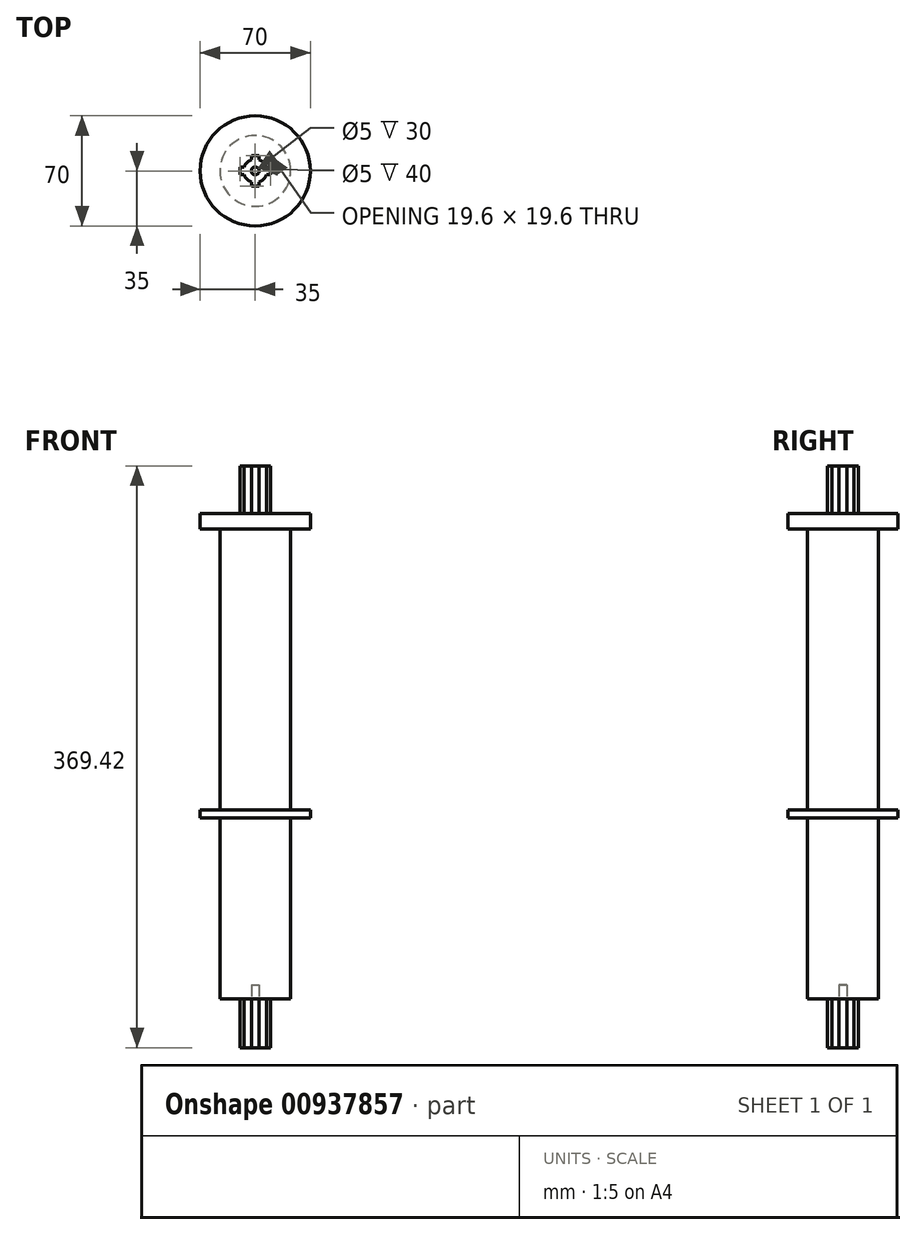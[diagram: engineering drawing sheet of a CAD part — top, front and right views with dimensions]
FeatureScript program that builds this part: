
annotation { "Feature Type Name" : "Feature", "Feature Type Description" : "" }
export const myFeature = defineFeature(function(context is Context, id is Id, definition is map)
    precondition{}
    {
        {
            var Q0;
            Q0=qCreatedBy(makeId("Top.planeOp"),FACE);
            var sketch = newSketch(context, id + "F0", { "sketchPlane" : qUnion([Q0])});
            skCircle(sketch, "E0", {"center": v(0, 0) * mm, "radius": 22.5 * mm});
            skSolve(sketch);
        }
        {
            var Q0;
            Q0=makeQuery(id+"F0.imprint","IMPRINT",FACE,{"disambiguationData":[TD([[makeQuery(id+"F0.imprint","IMPRINT",EDGE,{"derivedFrom":sQuery(id+"F0.wireOp",EDGE,"E0")}),1.0]])]});
            extrude(context, id + "F1", {"entities" : qUnion([Q0]), "depth" : 308.42 * mm, "offsetDistance" : 25 * mm});
        }
        {
            var Q0;
            Q0=makeQuery(id+"F1.opExtrude","CAP_FACE",FACE,{"disambiguationData":[OSD([sQuery(id+"F0.wireOp",EDGE,"E0")])],"isStart":false});
            var sketch = newSketch(context, id + "F2", { "sketchPlane" : qUnion([Q0])});
            skCircle(sketch, "E1", {"center": v(0, 0) * mm, "radius": 7.5 * mm});
            skLineSegment(sketch, "E2", {"start": v(0, 9.8) * mm, "end": v(-2.5, 9.8) * mm});
            skLineSegment(sketch, "E3", {"start": v(0, 9.8) * mm, "end": v(2.5, 9.8) * mm});
            skLineSegment(sketch, "E4", {"start": v(2.5, 9.8) * mm, "end": v(2.5, 7.07) * mm});
            skLineSegment(sketch, "E5", {"start": v(-2.5, 9.8) * mm, "end": v(-2.5, 7.07) * mm});
            skLineSegment(sketch, "E6.1.0", {"start": v(-9.8, 0) * mm, "end": v(-9.8, 2.5) * mm});
            skLineSegment(sketch, "E6.1.1", {"start": v(-9.8, 2.5) * mm, "end": v(-7.07, 2.5) * mm});
            skLineSegment(sketch, "E6.1.2", {"start": v(-9.8, 0) * mm, "end": v(-9.8, -2.5) * mm});
            skLineSegment(sketch, "E6.1.3", {"start": v(-9.8, -2.5) * mm, "end": v(-7.07, -2.5) * mm});
            skLineSegment(sketch, "E6.2.0", {"start": v(0, -9.8) * mm, "end": v(-2.5, -9.8) * mm});
            skLineSegment(sketch, "E6.2.1", {"start": v(-2.5, -9.8) * mm, "end": v(-2.5, -7.07) * mm});
            skLineSegment(sketch, "E6.2.2", {"start": v(0, -9.8) * mm, "end": v(2.5, -9.8) * mm});
            skLineSegment(sketch, "E6.2.3", {"start": v(2.5, -9.8) * mm, "end": v(2.5, -7.07) * mm});
            skLineSegment(sketch, "E6.3.0", {"start": v(9.8, 0) * mm, "end": v(9.8, -2.5) * mm});
            skLineSegment(sketch, "E6.3.1", {"start": v(9.8, -2.5) * mm, "end": v(7.07, -2.5) * mm});
            skLineSegment(sketch, "E6.3.2", {"start": v(9.8, 0) * mm, "end": v(9.8, 2.5) * mm});
            skLineSegment(sketch, "E6.3.3", {"start": v(9.8, 2.5) * mm, "end": v(7.07, 2.5) * mm});
            skSolve(sketch);
        }
        {
            var Q0;
            Q0=makeQuery(id+"F1.opExtrude","CAP_FACE",FACE,{"disambiguationData":[OSD([sQuery(id+"F0.wireOp",EDGE,"E0")])],"isStart":true});
            var sketch = newSketch(context, id + "F3", { "sketchPlane" : qUnion([Q0])});
            skCircle(sketch, "E7", {"center": v(0, 0) * mm, "radius": 7.5 * mm});
            skLineSegment(sketch, "E8", {"start": v(0, 9.8) * mm, "end": v(-2.5, 9.8) * mm});
            skLineSegment(sketch, "E9", {"start": v(0, 9.8) * mm, "end": v(2.5, 9.8) * mm});
            skLineSegment(sketch, "E10", {"start": v(2.5, 9.8) * mm, "end": v(2.5, 7.07) * mm});
            skLineSegment(sketch, "E11", {"start": v(-2.5, 9.8) * mm, "end": v(-2.5, 7.07) * mm});
            skLineSegment(sketch, "E12.1.0", {"start": v(-9.8, 0) * mm, "end": v(-9.8, 2.5) * mm});
            skLineSegment(sketch, "E12.1.1", {"start": v(-9.8, 2.5) * mm, "end": v(-7.07, 2.5) * mm});
            skLineSegment(sketch, "E12.1.2", {"start": v(-9.8, 0) * mm, "end": v(-9.8, -2.5) * mm});
            skLineSegment(sketch, "E12.1.3", {"start": v(-9.8, -2.5) * mm, "end": v(-7.07, -2.5) * mm});
            skLineSegment(sketch, "E12.2.0", {"start": v(0, -9.8) * mm, "end": v(-2.5, -9.8) * mm});
            skLineSegment(sketch, "E12.2.1", {"start": v(-2.5, -9.8) * mm, "end": v(-2.5, -7.07) * mm});
            skLineSegment(sketch, "E12.2.2", {"start": v(0, -9.8) * mm, "end": v(2.5, -9.8) * mm});
            skLineSegment(sketch, "E12.2.3", {"start": v(2.5, -9.8) * mm, "end": v(2.5, -7.07) * mm});
            skLineSegment(sketch, "E12.3.0", {"start": v(9.8, 0) * mm, "end": v(9.8, -2.5) * mm});
            skLineSegment(sketch, "E12.3.1", {"start": v(9.8, -2.5) * mm, "end": v(7.07, -2.5) * mm});
            skLineSegment(sketch, "E12.3.2", {"start": v(9.8, 0) * mm, "end": v(9.8, 2.5) * mm});
            skLineSegment(sketch, "E12.3.3", {"start": v(9.8, 2.5) * mm, "end": v(7.07, 2.5) * mm});
            skSolve(sketch);
        }
        {
            var Q0;
            Q0=makeQuery(id+"F3.imprint","IMPRINT",FACE,{"disambiguationData":[TD([[makeQuery(id+"F3.imprint","IMPRINT",EDGE,{"derivedFrom":sQuery(id+"F3.wireOp",EDGE,"E12.3.0")}),-1.0]])]});
            var Q1;
            Q1=makeQuery(id+"F3.imprint","IMPRINT",FACE,{"disambiguationData":[TD([[makeQuery(id+"F3.imprint","IMPRINT",EDGE,{"derivedFrom":sQuery(id+"F3.wireOp",EDGE,"E12.2.0")}),-1.0]])]});
            var Q2;
            Q2=makeQuery(id+"F3.imprint","IMPRINT",FACE,{"disambiguationData":[TD([[makeQuery(id+"F3.imprint","IMPRINT",EDGE,{"derivedFrom":sQuery(id+"F3.wireOp",EDGE,"E12.1.0")}),-1.0]])]});
            var Q3;
            {var subQ0=sQuery(id+"F3.wireOp",EDGE,"E7");var subQ4=makeQuery(id+"F3.imprint","INTERSECT",VERTEX,{"derivedFrom":[subQ0,sQuery(id+"F3.wireOp",EDGE,"E10")]});Q3=makeQuery(id+"F3.imprint","IMPRINT",FACE,{"disambiguationData":[TD([[makeQuery(id+"F3.imprint","IMPRINT",EDGE,{"disambiguationData":[TD([[subQ4,1.0]])],"derivedFrom":subQ0}),1.0]])]});}
            var Q4;
            Q4=makeQuery(id+"F3.imprint","IMPRINT",FACE,{"disambiguationData":[TD([[makeQuery(id+"F3.imprint","IMPRINT",EDGE,{"derivedFrom":sQuery(id+"F3.wireOp",EDGE,"E8")}),1.0]])]});
            extrude(context, id + "F4", {"entities" : qUnion([Q0, Q1, Q2, Q3, Q4]), "operationType" : NewBodyOperationType.ADD, "depth" : 31 * mm, "offsetDistance" : 25 * mm});
        }
        {
            var Q0;
            Q0=makeQuery(id+"F4.opExtrude","CAP_FACE",FACE,{"disambiguationData":[OSD([sQuery(id+"F3.wireOp",EDGE,"E7"),sQuery(id+"F3.wireOp",EDGE,"E8"),sQuery(id+"F3.wireOp",EDGE,"E9"),sQuery(id+"F3.wireOp",EDGE,"E10"),sQuery(id+"F3.wireOp",EDGE,"E11"),sQuery(id+"F3.wireOp",EDGE,"E12.1.0"),sQuery(id+"F3.wireOp",EDGE,"E12.1.1"),sQuery(id+"F3.wireOp",EDGE,"E12.1.2"),sQuery(id+"F3.wireOp",EDGE,"E12.1.3"),sQuery(id+"F3.wireOp",EDGE,"E12.2.0"),sQuery(id+"F3.wireOp",EDGE,"E12.2.1"),sQuery(id+"F3.wireOp",EDGE,"E12.2.2"),sQuery(id+"F3.wireOp",EDGE,"E12.2.3"),sQuery(id+"F3.wireOp",EDGE,"E12.3.0"),sQuery(id+"F3.wireOp",EDGE,"E12.3.1"),sQuery(id+"F3.wireOp",EDGE,"E12.3.2"),sQuery(id+"F3.wireOp",EDGE,"E12.3.3")])],"isStart":false});
            var sketch = newSketch(context, id + "F5", { "sketchPlane" : qUnion([Q0])});
            skCircle(sketch, "E13", {"center": v(0, 0) * mm, "radius": 2.5 * mm});
            skSolve(sketch);
        }
        {
            var Q0;
            Q0=qSketchRegion(id+"F5",true);
            extrude(context, id + "F6", {"entities" : qUnion([Q0]), "operationType" : NewBodyOperationType.REMOVE, "oppositeDirection" : true, "depth" : 40 * mm, "offsetDistance" : 25 * mm});
        }
        {
            var Q0;
            {var subQ0=sQuery(id+"F2.wireOp",EDGE,"E1");var subQ4=makeQuery(id+"F2.imprint","INTERSECT",VERTEX,{"derivedFrom":[subQ0,sQuery(id+"F2.wireOp",EDGE,"E4")]});Q0=makeQuery(id+"F2.imprint","IMPRINT",FACE,{"disambiguationData":[TD([[makeQuery(id+"F2.imprint","IMPRINT",EDGE,{"disambiguationData":[TD([[subQ4,1.0]])],"derivedFrom":subQ0}),1.0]])]});}
            var Q1;
            Q1=makeQuery(id+"F2.imprint","IMPRINT",FACE,{"disambiguationData":[TD([[makeQuery(id+"F2.imprint","IMPRINT",EDGE,{"derivedFrom":sQuery(id+"F2.wireOp",EDGE,"E6.1.0")}),-1.0]])]});
            var Q2;
            Q2=makeQuery(id+"F2.imprint","IMPRINT",FACE,{"disambiguationData":[TD([[makeQuery(id+"F2.imprint","IMPRINT",EDGE,{"derivedFrom":sQuery(id+"F2.wireOp",EDGE,"E2")}),1.0]])]});
            var Q3;
            Q3=makeQuery(id+"F2.imprint","IMPRINT",FACE,{"disambiguationData":[TD([[makeQuery(id+"F2.imprint","IMPRINT",EDGE,{"derivedFrom":sQuery(id+"F2.wireOp",EDGE,"E6.3.0")}),-1.0]])]});
            var Q4;
            Q4=makeQuery(id+"F2.imprint","IMPRINT",FACE,{"disambiguationData":[TD([[makeQuery(id+"F2.imprint","IMPRINT",EDGE,{"derivedFrom":sQuery(id+"F2.wireOp",EDGE,"E6.2.0")}),-1.0]])]});
            extrude(context, id + "F7", {"entities" : qUnion([Q0, Q1, Q2, Q3, Q4]), "operationType" : NewBodyOperationType.ADD, "depth" : 30 * mm, "offsetDistance" : 25 * mm});
        }
        {
            var Q0;
            Q0=makeQuery(id+"F7.opExtrude","CAP_FACE",FACE,{"disambiguationData":[OSD([sQuery(id+"F2.wireOp",EDGE,"E1"),sQuery(id+"F2.wireOp",EDGE,"E2"),sQuery(id+"F2.wireOp",EDGE,"E3"),sQuery(id+"F2.wireOp",EDGE,"E4"),sQuery(id+"F2.wireOp",EDGE,"E5"),sQuery(id+"F2.wireOp",EDGE,"E6.1.0"),sQuery(id+"F2.wireOp",EDGE,"E6.1.1"),sQuery(id+"F2.wireOp",EDGE,"E6.1.2"),sQuery(id+"F2.wireOp",EDGE,"E6.1.3"),sQuery(id+"F2.wireOp",EDGE,"E6.2.0"),sQuery(id+"F2.wireOp",EDGE,"E6.2.1"),sQuery(id+"F2.wireOp",EDGE,"E6.2.2"),sQuery(id+"F2.wireOp",EDGE,"E6.2.3"),sQuery(id+"F2.wireOp",EDGE,"E6.3.0"),sQuery(id+"F2.wireOp",EDGE,"E6.3.1"),sQuery(id+"F2.wireOp",EDGE,"E6.3.2"),sQuery(id+"F2.wireOp",EDGE,"E6.3.3")])],"isStart":false});
            var sketch = newSketch(context, id + "F8", { "sketchPlane" : qUnion([Q0])});
            skCircle(sketch, "E14", {"center": v(0, 0) * mm, "radius": 2.5 * mm});
            skSolve(sketch);
        }
        {
            var Q0;
            Q0=qSketchRegion(id+"F8",true);
            extrude(context, id + "F9", {"entities" : qUnion([Q0]), "operationType" : NewBodyOperationType.REMOVE, "oppositeDirection" : true, "depth" : 30 * mm, "offsetDistance" : 25 * mm});
        }
        {
            var Q0;
            Q0=makeQuery(id+"F1.opExtrude","CAP_FACE",FACE,{"disambiguationData":[OSD([sQuery(id+"F0.wireOp",EDGE,"E0")])],"isStart":false});
            var sketch = newSketch(context, id + "F10", { "sketchPlane" : qUnion([Q0])});
            skCircle(sketch, "E15", {"center": v(0, 0) * mm, "radius": 35 * mm});
            skSolve(sketch);
        }
        {
            var Q0;
            Q0=qSketchRegion(id+"F10",true);
            extrude(context, id + "F11", {"entities" : qUnion([Q0]), "operationType" : NewBodyOperationType.ADD, "oppositeDirection" : true, "depth" : 10 * mm, "offsetDistance" : 25 * mm});
        }
        {
            var Q0;
            Q0=qCreatedBy(makeId("Top.planeOp"),FACE);
            cPlane(context, id + "F12", {"entities" : qUnion([Q0]), "cplaneType" : CPlaneType.OFFSET, "offset" : 115 * mm, "width" : 150 * mm, "height" : 150 * mm});
        }
        {
            var Q0;
            Q0=qCreatedBy(id+"F12.planeOp",FACE);
            var sketch = newSketch(context, id + "F13", { "sketchPlane" : qUnion([Q0])});
            skCircle(sketch, "E16", {"center": v(0, 0) * mm, "radius": 35 * mm});
            skSolve(sketch);
        }
        {
            var Q0;
            Q0=makeQuery(id+"F13.imprint","IMPRINT",FACE,{"disambiguationData":[TD([[makeQuery(id+"F13.imprint","IMPRINT",EDGE,{"derivedFrom":sQuery(id+"F13.wireOp",EDGE,"E16")}),1.0]])]});
            extrude(context, id + "F14", {"entities" : qUnion([Q0]), "operationType" : NewBodyOperationType.ADD, "depth" : 5 * mm, "offsetDistance" : 25 * mm});
        }
    });
